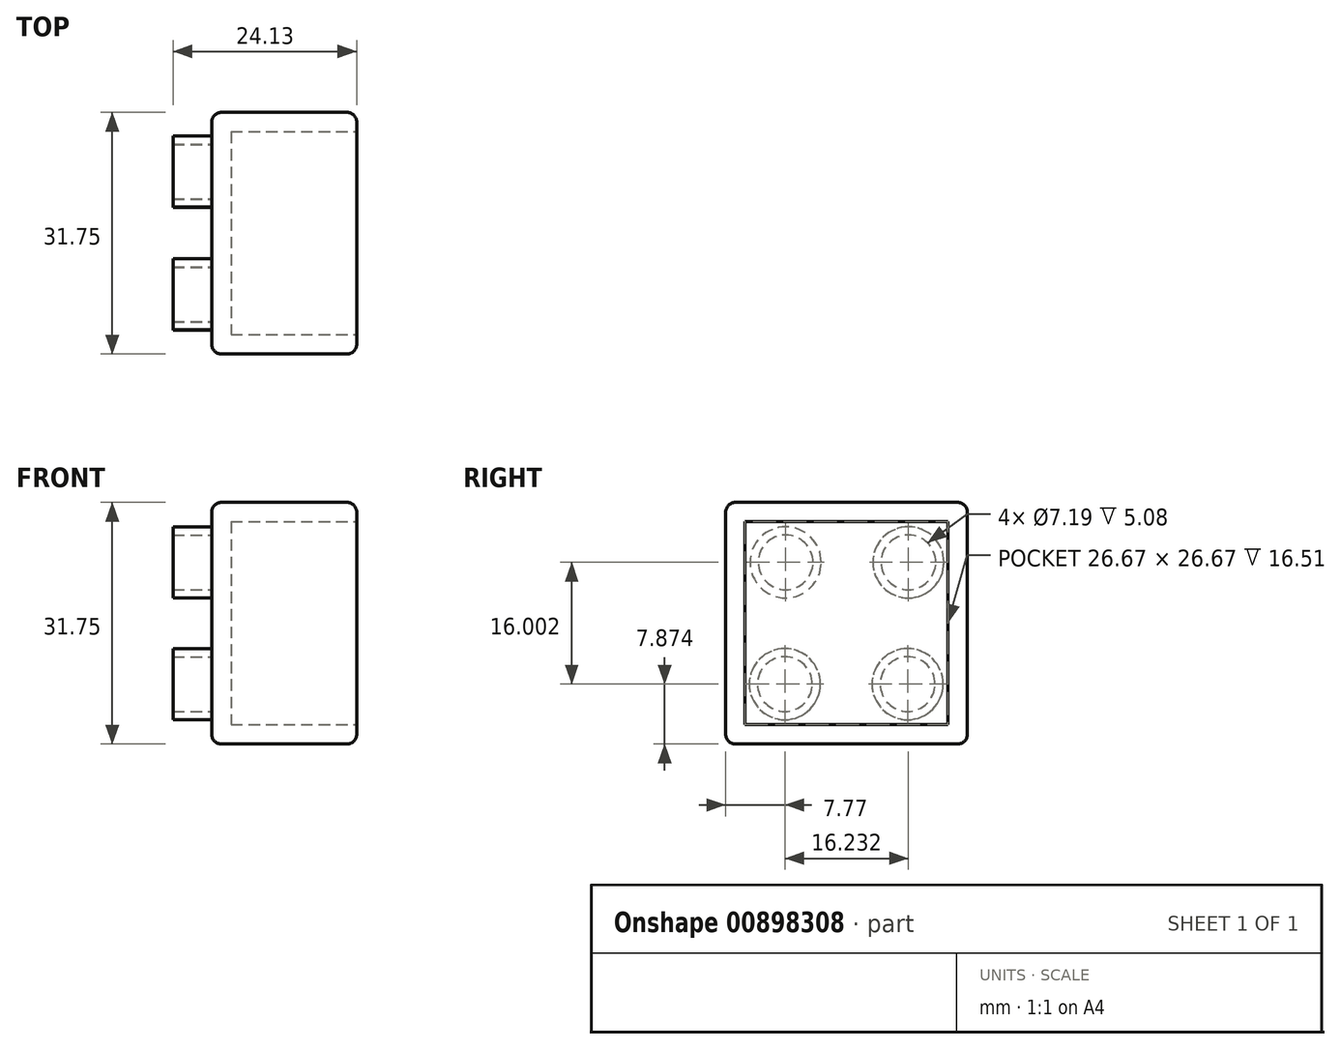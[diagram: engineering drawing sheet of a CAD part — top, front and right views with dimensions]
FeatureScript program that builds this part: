
annotation { "Feature Type Name" : "Feature", "Feature Type Description" : "" }
export const myFeature = defineFeature(function(context is Context, id is Id, definition is map)
    precondition{}
    {
        {
            var Q0;
            Q0=qCreatedBy(makeId("Top.planeOp"),FACE);
            var sketch = newSketch(context, id + "F0", { "sketchPlane" : qUnion([Q0])});
            skLineSegment(sketch, "E0.bottom", {"start": v(-24.35, 4.54) * mm, "end": v(-5.3, 4.54) * mm});
            skLineSegment(sketch, "E0.top", {"start": v(-24.35, -27.21) * mm, "end": v(-5.3, -27.21) * mm});
            skLineSegment(sketch, "E0.left", {"start": v(-24.35, 4.54) * mm, "end": v(-24.35, -27.21) * mm});
            skLineSegment(sketch, "E0.right", {"start": v(-5.3, 4.54) * mm, "end": v(-5.3, -27.21) * mm});
            skSolve(sketch);
        }
        {
            var Q0;
            Q0 = qSketchRegion(id + "F0", true);
            var Q1;
            Q1 = qSketchRegion(id + "F3", true);
            extrude(context, id + "F1", {"entities" : qUnion([Q0, Q1]), "depth" : 31.75 * mm, "offsetDistance" : 25.4 * mm});
        }
        {
            var Q0;
            Q0=makeQuery(id+"F1.opExtrude","SWEPT_FACE",FACE,{"disambiguationData":[OSD([sQuery(id+"F0.wireOp",EDGE,"E0.right")])]});
            shell(context, id + "F2", {"entities" : qUnion([Q0]), "thickness" : 2.54 * mm});
        }
        {
            var Q0;
            Q0=makeQuery(id+"F1.opExtrude","SWEPT_FACE",FACE,{"disambiguationData":[OSD([sQuery(id+"F0.wireOp",EDGE,"E0.left")])]});
            var sketch = newSketch(context, id + "F3", { "sketchPlane" : qUnion([Q0])});
            skSolve(sketch);
        }
        {
            var Q0;
            {var subQ0=sQuery(id+"F0.wireOp",EDGE,"E0.left");Q0=makeQuery(id+"F3.imprint","IMPRINT",FACE,{"disambiguationData":[TD([[makeQuery(id+"F3.imprint","IMPRINT",EDGE,{"derivedFrom":makeQuery(id+"F1.opExtrude","CAP_EDGE",EDGE,{"disambiguationData":[OSD([subQ0])],"isStart":true})}),1.0]])]});}
            var sketch = newSketch(context, id + "F4", { "sketchPlane" : qUnion([Q0])});
            skCircle(sketch, "E1", {"center": v(19.34, 23.88) * mm, "radius": 4.67 * mm});
            skCircle(sketch, "E2", {"center": v(19.34, 23.88) * mm, "radius": 3.6 * mm});
            skCircle(sketch, "E3.1.0.0", {"center": v(3.2, 23.88) * mm, "radius": 4.67 * mm});
            skCircle(sketch, "E3.1.0.1", {"center": v(3.2, 23.88) * mm, "radius": 3.6 * mm});
            skLineSegment(sketch, "E3.direction1", {"start": v(19.34, 23.88) * mm, "end": v(3.2, 23.88) * mm, "construction": true});
            skCircle(sketch, "E4.2.0.0", {"center": v(3.31, 7.87) * mm, "radius": 3.6 * mm});
            skCircle(sketch, "E4.2.0.1", {"center": v(3.31, 7.87) * mm, "radius": 4.67 * mm});
            skCircle(sketch, "E4.3.0.0", {"center": v(19.44, 7.87) * mm, "radius": 3.6 * mm});
            skCircle(sketch, "E4.3.0.1", {"center": v(19.44, 7.87) * mm, "radius": 4.67 * mm});
            skSolve(sketch);
        }
        {
            var Q0;
            Q0 = qSketchRegion(id + "F4", true);
            extrude(context, id + "F5", {"entities" : qUnion([Q0]), "operationType" : NewBodyOperationType.ADD, "depth" : 5.08 * mm, "offsetDistance" : 25.4 * mm});
        }
        {
            var Q0;
            Q0=makeQuery(id+"F1.opExtrude","CAP_FACE",FACE,{"disambiguationData":[OSD([sQuery(id+"F0.wireOp",EDGE,"E0.bottom"),sQuery(id+"F0.wireOp",EDGE,"E0.top"),sQuery(id+"F0.wireOp",EDGE,"E0.left"),sQuery(id+"F0.wireOp",EDGE,"E0.right")])],"isStart":true});
            var Q1;
            Q1=makeQuery(id+"F1.opExtrude","SWEPT_EDGE",EDGE,{"disambiguationData":[OSD([sQuery(id+"F0.wireOp",EDGE,"E0.top"),sQuery(id+"F0.wireOp",EDGE,"E0.left")])]});
            var Q2;
            Q2=makeQuery(id+"F1.opExtrude","CAP_FACE",FACE,{"disambiguationData":[OSD([sQuery(id+"F0.wireOp",EDGE,"E0.bottom"),sQuery(id+"F0.wireOp",EDGE,"E0.top"),sQuery(id+"F0.wireOp",EDGE,"E0.left"),sQuery(id+"F0.wireOp",EDGE,"E0.right")])],"isStart":false});
            var Q3;
            Q3=makeQuery(id+"F1.opExtrude","SWEPT_FACE",FACE,{"disambiguationData":[OSD([sQuery(id+"F0.wireOp",EDGE,"E0.top")])]});
            var Q4;
            Q4=makeQuery(id+"F1.opExtrude","SWEPT_FACE",FACE,{"disambiguationData":[OSD([sQuery(id+"F0.wireOp",EDGE,"E0.bottom")])]});
            fillet(context, id + "F6", {"entities" : qUnion([Q0, Q1, Q2, Q3, Q4]), "radius" : 1.27 * mm, "tangentPropagation" : true, "allowEdgeOverflow" : false});
        }
    });
